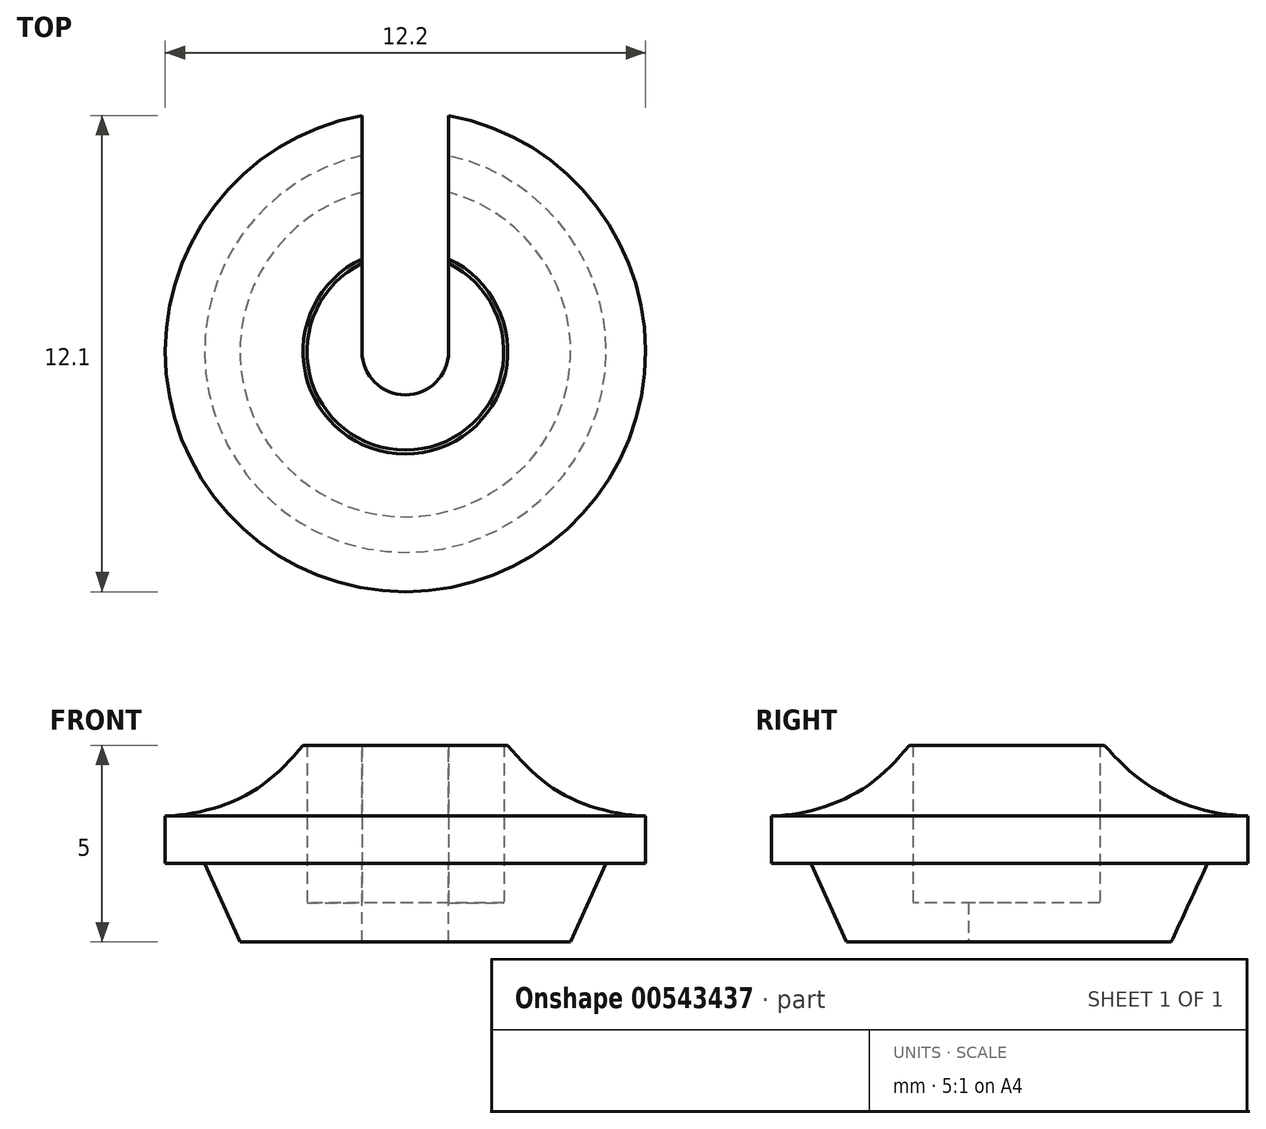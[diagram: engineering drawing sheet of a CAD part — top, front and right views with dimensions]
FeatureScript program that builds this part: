
annotation { "Feature Type Name" : "Feature", "Feature Type Description" : "" }
export const myFeature = defineFeature(function(context is Context, id is Id, definition is map)
    precondition{}
    {
        {
            var Q0;
            Q0=qCreatedBy(makeId("Front.planeOp"),FACE);
            var sketch = newSketch(context, id + "F0", { "sketchPlane" : qUnion([Q0])});
            skLineSegment(sketch, "E0", {"start": v(0, -3.7) * mm, "end": v(0, 5.15) * mm, "construction": true});
            skLineSegment(sketch, "E1", {"start": v(1.1, -1.86) * mm, "end": v(1.1, -0.86) * mm});
            skLineSegment(sketch, "E2", {"start": v(1.1, -0.86) * mm, "end": v(2.5, -0.86) * mm});
            skLineSegment(sketch, "E3", {"start": v(2.5, -0.86) * mm, "end": v(2.5, 3.14) * mm});
            skLineSegment(sketch, "E4", {"start": v(2.5, 3.14) * mm, "end": v(2.6, 3.14) * mm});
            skFitSpline(sketch, "E5", {"points": [v(2.6, 3.14) * mm, v(3.92, 1.95) * mm, v(6.1, 1.34) * mm], "startDerivative": vector(2.5, -3.01) * mm, "endDerivative": vector(4.51, -0.16) * mm});
            skLineSegment(sketch, "E6", {"start": v(6.1, 1.34) * mm, "end": v(6.1, 0.14) * mm});
            skLineSegment(sketch, "E7", {"start": v(6.1, 0.14) * mm, "end": v(5.1, 0.14) * mm});
            skLineSegment(sketch, "E8", {"start": v(5.1, 0.14) * mm, "end": v(4.2, -1.86) * mm});
            skLineSegment(sketch, "E9", {"start": v(4.2, -1.86) * mm, "end": v(1.1, -1.86) * mm});
            skLineSegment(sketch, "E10", {"start": v(0, -1.02) * mm, "end": v(1.1, -1.02) * mm, "construction": true});
            skLineSegment(sketch, "E11", {"start": v(0, 0.46) * mm, "end": v(2.5, 0.46) * mm, "construction": true});
            skLineSegment(sketch, "E12", {"start": v(6.1, 0.74) * mm, "end": v(1.1, 0.74) * mm, "construction": true});
            skSolve(sketch);
        }
        {
            var Q0;
            Q0 = qSketchRegion(id + "F0", true);
            var Q1;
            Q1=sQuery(id+"F0.wireOp",EDGE,"E0");
            revolve(context, id + "F1", {"entities" : qUnion([Q0]), "axis" : qUnion([Q1]), "revolveType" : RevolveType.FULL});
        }
        {
            var Q0;
            Q0=qCreatedBy(makeId("Front.planeOp"),FACE);
            var sketch = newSketch(context, id + "F2", { "sketchPlane" : qUnion([Q0])});
            skLineSegment(sketch, "E13.0", {"start": v(1.1, -1.86) * mm, "end": v(1.1, -0.86) * mm});
            skLineSegment(sketch, "E14.bottom", {"start": v(0, -3.7) * mm, "end": v(1.1, -3.7) * mm});
            skLineSegment(sketch, "E14.top", {"start": v(0, 3.78) * mm, "end": v(1.1, 3.78) * mm});
            skLineSegment(sketch, "E14.right", {"start": v(1.1, -3.7) * mm, "end": v(1.1, 3.78) * mm});
            skLineSegment(sketch, "E15.bottom", {"start": v(0, -3.7) * mm, "end": v(-1.1, -3.7) * mm});
            skLineSegment(sketch, "E15.top", {"start": v(0, 3.78) * mm, "end": v(-1.1, 3.78) * mm});
            skLineSegment(sketch, "E15.right", {"start": v(-1.1, -3.7) * mm, "end": v(-1.1, 3.78) * mm});
            skSolve(sketch);
        }
        {
            var Q0;
            Q0 = qSketchRegion(id + "F2", true);
            extrude(context, id + "F3", {"entities" : qUnion([Q0]), "operationType" : NewBodyOperationType.REMOVE, "oppositeDirection" : true, "depth" : 25 * mm, "offsetDistance" : 25 * mm});
        }
    });
